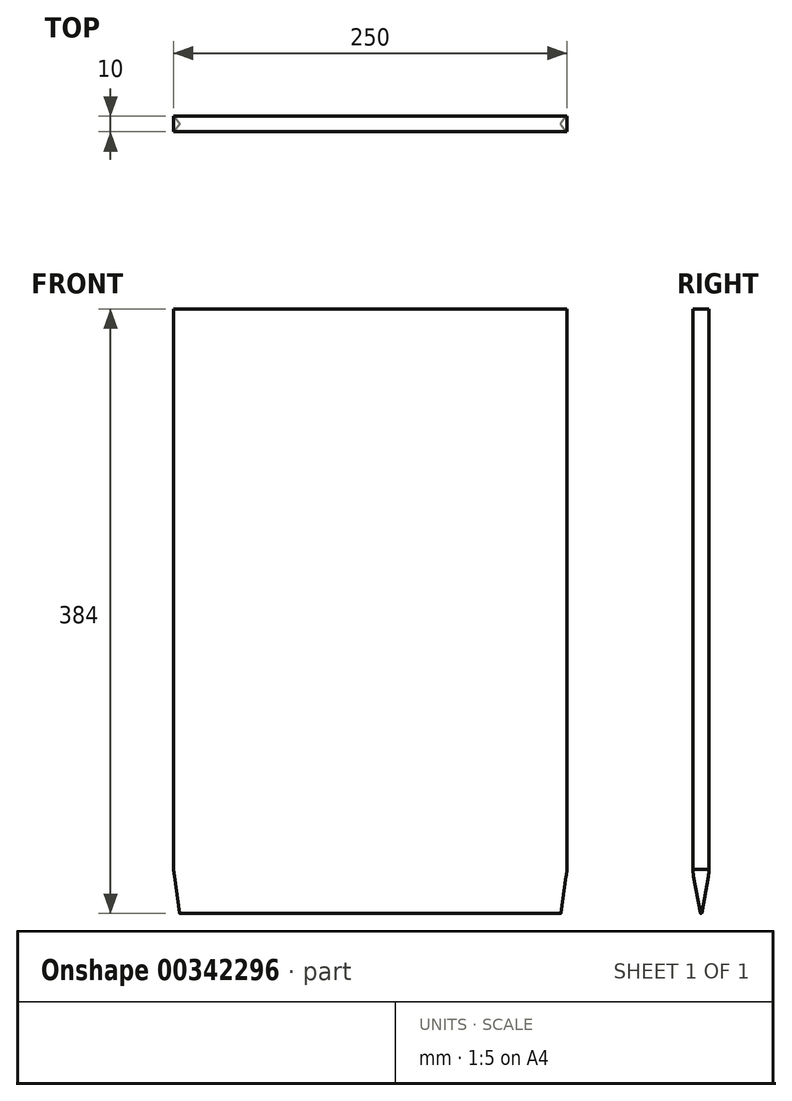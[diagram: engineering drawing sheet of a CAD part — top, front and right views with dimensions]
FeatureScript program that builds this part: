
annotation { "Feature Type Name" : "Feature", "Feature Type Description" : "" }
export const myFeature = defineFeature(function(context is Context, id is Id, definition is map)
    precondition{}
    {
        {
            var Q0;
            Q0=qCreatedBy(makeId("Right.planeOp"),FACE);
            var sketch = newSketch(context, id + "F0", { "sketchPlane" : qUnion([Q0])});
            skLineSegment(sketch, "E0.bottom", {"start": v(5, 210) * mm, "end": v(-5, 210) * mm});
            skLineSegment(sketch, "E0.top", {"start": v(5, -210) * mm, "end": v(-5, -210) * mm});
            skLineSegment(sketch, "E0.left", {"start": v(5, 210) * mm, "end": v(5, -182.83) * mm});
            skLineSegment(sketch, "E0.right", {"start": v(-5, 210) * mm, "end": v(-5, -182.83) * mm});
            skPoint(sketch, "E0.middle", {"position": v(0, 0) * mm});
            skPoint(sketch, "E1", {"position": v(0, -210) * mm});
            skCircle(sketch, "E2", {"center": v(0, -209.5) * mm, "radius": 0.5 * mm});
            skLineSegment(sketch, "E3", {"start": v(-4.67, -186.38) * mm, "end": v(-0.5, -209.59) * mm});
            skLineSegment(sketch, "E4", {"start": v(0.5, -209.59) * mm, "end": v(4.69, -186.4) * mm});
            skPoint(sketch, "E5.newPointB", {"position": v(-6.67, -175.28) * mm});
            skArc(sketch, "E5.filletArc", {"start": v(-5, -182.83) * mm, "mid": v(-4.91, -184.61) * mm, "end": v(-4.67, -186.38) * mm});
            skPoint(sketch, "E6.newPointA", {"position": v(5, -282.92) * mm});
            skPoint(sketch, "E6.newPointB", {"position": v(6.7, -175.28) * mm});
            skArc(sketch, "E6.filletArc", {"start": v(4.69, -186.4) * mm, "mid": v(4.93, -184.62) * mm, "end": v(5, -182.83) * mm});
            skSolve(sketch);
        }
        {
            var Q0;
            {var subQ4=sQuery(id+"F0.wireOp",EDGE,"E0.bottom");Q0=makeQuery(id+"F0.imprint","IMPRINT",FACE,{"disambiguationData":[TD([[makeQuery(id+"F0.imprint","IMPRINT",EDGE,{"derivedFrom":subQ4}),1.0]])]});}
            var Q1;
            {var subQ0=sQuery(id+"F0.wireOp",EDGE,"E2");var subQ1=makeQuery(id+"F0.imprint","INTERSECT",VERTEX,{"derivedFrom":[subQ0,sQuery(id+"F0.wireOp",EDGE,"E3")]});Q1=makeQuery(id+"F0.imprint","IMPRINT",FACE,{"disambiguationData":[TD([[makeQuery(id+"F0.imprint","IMPRINT",EDGE,{"disambiguationData":[TD([[subQ1,-1.0]])],"derivedFrom":subQ0}),1.0]])]});}
            extrude(context, id + "F1", {"entities" : qUnion([Q0, Q1]), "endBound" : BoundingType.SYMMETRIC, "depth" : 250 * mm, "offsetDistance" : 25 * mm});
        }
        {
            var Q0;
            Q0=makeQuery(id+"F1.opExtrude","SWEPT_FACE",FACE,{"disambiguationData":[OSD([sQuery(id+"F0.wireOp",EDGE,"E0.left")])]});
            var sketch = newSketch(context, id + "F2", { "sketchPlane" : qUnion([Q0])});
            skLineSegment(sketch, "E7", {"start": v(-125, -182) * mm, "end": v(-121, -210) * mm});
            skLineSegment(sketch, "E8", {"start": v(-125.1, -210) * mm, "end": v(-121, -210) * mm});
            skLineSegment(sketch, "E9", {"start": v(-125, -182) * mm, "end": v(-125.1, -210) * mm});
            skLineSegment(sketch, "E10.MirrorCS", {"start": v(125, -182) * mm, "end": v(121, -210) * mm});
            skLineSegment(sketch, "E11.MirrorCS", {"start": v(125, -182) * mm, "end": v(125.1, -210) * mm});
            skLineSegment(sketch, "E12.MirrorCS", {"start": v(125.1, -210) * mm, "end": v(121, -210) * mm});
            skCircle(sketch, "E13", {"center": v(0, 198) * mm, "radius": 4 * mm});
            skCircle(sketch, "E14", {"center": v(0, 180) * mm, "radius": 4 * mm});
            skSolve(sketch);
        }
        {
            var Q0;
            Q0=qSketchRegion(id+"F2",true);
            extrude(context, id + "F3", {"entities" : qUnion([Q0]), "operationType" : NewBodyOperationType.REMOVE, "oppositeDirection" : true, "depth" : 25 * mm});
        }
        {
            var Q0;
            Q0=makeQuery(id+"F1.opExtrude","SWEPT_FACE",FACE,{"disambiguationData":[OSD([sQuery(id+"F0.wireOp",EDGE,"E0.bottom")])]});
            extrude(context, id + "F4", {"entities" : qUnion([Q0]), "operationType" : NewBodyOperationType.REMOVE, "oppositeDirection" : true, "depth" : 36 * mm, "offsetDistance" : 25 * mm});
        }
    });
